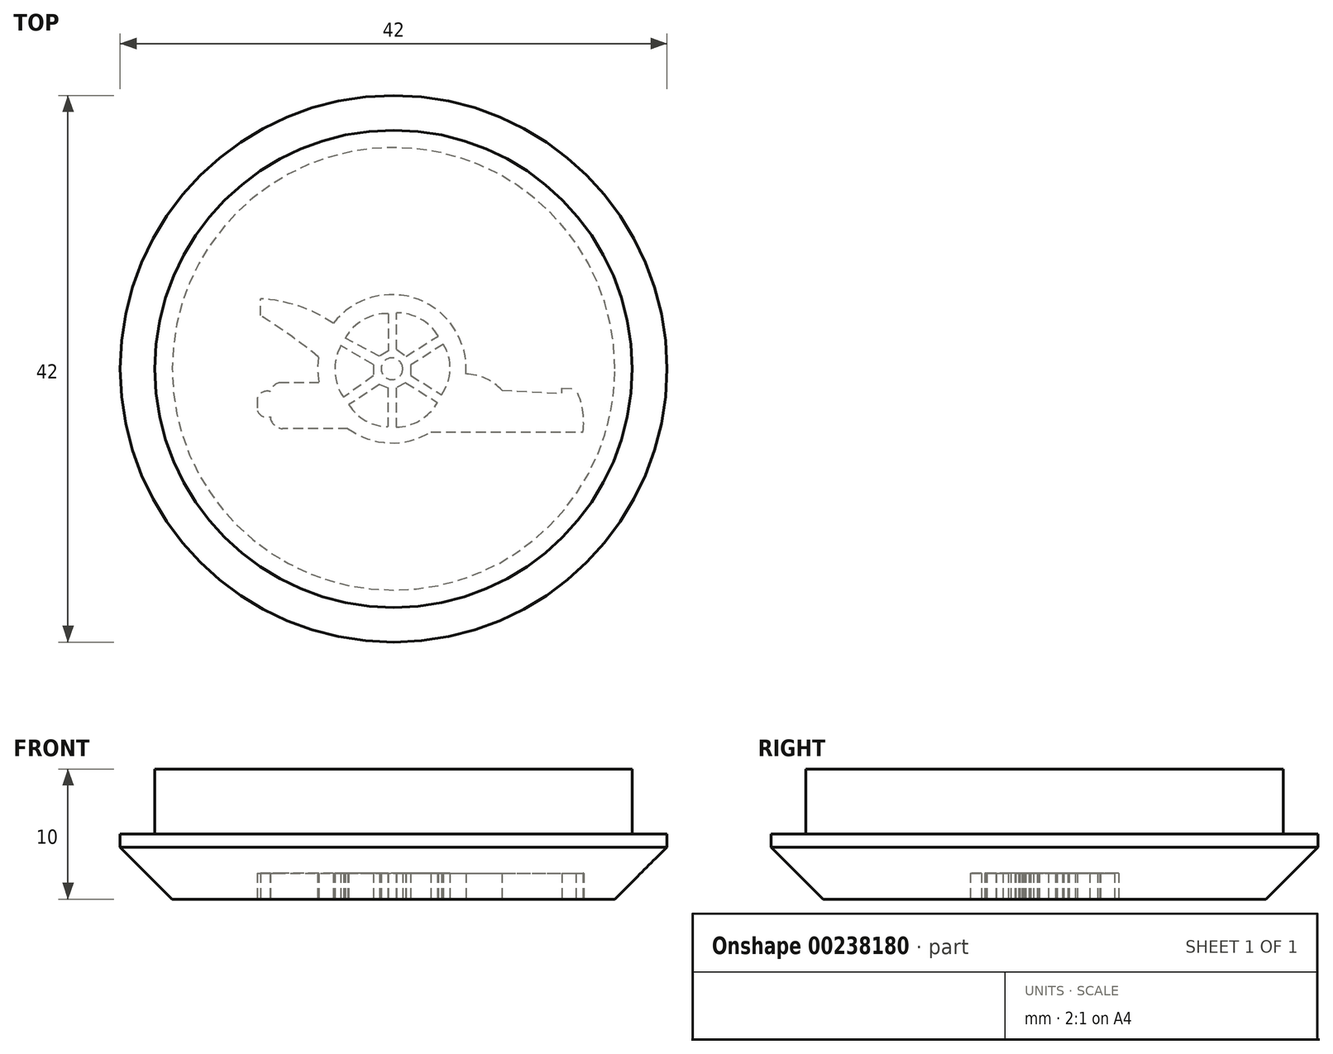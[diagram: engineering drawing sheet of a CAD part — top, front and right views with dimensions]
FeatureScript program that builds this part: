
annotation { "Feature Type Name" : "Feature", "Feature Type Description" : "" }
export const myFeature = defineFeature(function(context is Context, id is Id, definition is map)
    precondition{}
    {
        {
            var Q0;
            Q0=qCreatedBy(makeId("Top.planeOp"),FACE);
            var sketch = newSketch(context, id + "F0", { "sketchPlane" : qUnion([Q0])});
            skCircle(sketch, "E0", {"center": v(0, 0) * mm, "radius": 21 * mm});
            skSolve(sketch);
        }
        {
            var Q0;
            Q0=makeQuery(id+"F0.imprint","IMPRINT",FACE,{"disambiguationData":[TD([[makeQuery(id+"F0.imprint","IMPRINT",EDGE,{"derivedFrom":sQuery(id+"F0.wireOp",EDGE,"E0")}),1.0]])]});
            extrude(context, id + "F1", {"entities" : qUnion([Q0]), "depth" : 5 * mm, "offsetDistance" : 25 * mm});
        }
        {
            var Q0;
            Q0=makeQuery(id+"F1.opExtrude","CAP_FACE",FACE,{"disambiguationData":[OSD([sQuery(id+"F0.wireOp",EDGE,"E0")])],"isStart":false});
            var sketch = newSketch(context, id + "F2", { "sketchPlane" : qUnion([Q0])});
            skCircle(sketch, "E1", {"center": v(0, 0) * mm, "radius": 18.33 * mm});
            skSolve(sketch);
        }
        {
            var Q0;
            Q0=makeQuery(id+"F2.imprint","IMPRINT",FACE,{"disambiguationData":[TD([[makeQuery(id+"F2.imprint","IMPRINT",EDGE,{"derivedFrom":sQuery(id+"F2.wireOp",EDGE,"E1")}),1.0]])]});
            extrude(context, id + "F3", {"entities" : qUnion([Q0]), "operationType" : NewBodyOperationType.ADD, "depth" : 5 * mm, "offsetDistance" : 25 * mm});
        }
        {
            var Q0;
            Q0=makeQuery(id+"F1.opExtrude","CAP_FACE",FACE,{"disambiguationData":[OSD([sQuery(id+"F0.wireOp",EDGE,"E0")])],"isStart":true});
            var sketch = newSketch(context, id + "F4", { "sketchPlane" : qUnion([Q0])});
            skLineSegment(sketch, "E2", {"start": v(-5.73, 1.06) * mm, "end": v(-8.6, 1.06) * mm});
            skLineSegment(sketch, "E3", {"start": v(-3.5, 4.6) * mm, "end": v(-8.52, 4.6) * mm});
            skArc(sketch, "E4", {"start": v(-9.47, 1.74) * mm, "mid": v(-9.15, 1.25) * mm, "end": v(-8.6, 1.06) * mm});
            skArc(sketch, "E5", {"start": v(-8.52, 4.6) * mm, "mid": v(-9.18, 4.33) * mm, "end": v(-9.47, 3.69) * mm});
            skLineSegment(sketch, "E6", {"start": v(-10.48, 2.26) * mm, "end": v(-10.48, 3.2) * mm});
            skArc(sketch, "E7", {"start": v(-10.48, 2.26) * mm, "mid": v(-10.07, 1.81) * mm, "end": v(-9.47, 1.74) * mm});
            skArc(sketch, "E8", {"start": v(-9.47, 3.69) * mm, "mid": v(-10.07, 3.65) * mm, "end": v(-10.48, 3.2) * mm});
            skCircle(sketch, "E9", {"center": v(-0.13, 0) * mm, "radius": 5.7 * mm});
            skCircle(sketch, "E10", {"center": v(-0.13, 0) * mm, "radius": 0.83 * mm});
            skArc(sketch, "E11", {"start": v(-10.22, -4.09) * mm, "mid": v(-7.94, -2.56) * mm, "end": v(-5.76, -0.9) * mm});
            skLineSegment(sketch, "E12", {"start": v(-10.22, -4.09) * mm, "end": v(-10.22, -5.37) * mm});
            skArc(sketch, "E13", {"start": v(-10.22, -5.37) * mm, "mid": v(-7.3, -4.82) * mm, "end": v(-4.64, -3.49) * mm});
            skArc(sketch, "E14", {"start": v(5.56, 0.4) * mm, "mid": v(7.08, 0.74) * mm, "end": v(8.33, 1.66) * mm});
            skLineSegment(sketch, "E15", {"start": v(8.33, 1.66) * mm, "end": v(12.92, 1.88) * mm});
            skLineSegment(sketch, "E16", {"start": v(12.92, 1.88) * mm, "end": v(12.94, 1.49) * mm});
            skLineSegment(sketch, "E17", {"start": v(12.94, 1.49) * mm, "end": v(14, 1.54) * mm});
            skLineSegment(sketch, "E18", {"start": v(2.88, 4.84) * mm, "end": v(14.55, 4.84) * mm});
            skArc(sketch, "E19", {"start": v(14, 1.54) * mm, "mid": v(14.52, 3.15) * mm, "end": v(14.55, 4.84) * mm});
            skArc(sketch, "E20", {"start": v(-3.26, -2.55) * mm, "mid": v(-2.14, -3.5) * mm, "end": v(-0.77, -4.06) * mm});
            skLineSegment(sketch, "E21", {"start": v(-1.56, -0.31) * mm, "end": v(-1.56, 0.55) * mm});
            skLineSegment(sketch, "E22", {"start": v(-1.56, 0.55) * mm, "end": v(-3.84, 2.2) * mm});
            skLineSegment(sketch, "E23", {"start": v(-1.56, -0.31) * mm, "end": v(-4.04, -1.78) * mm});
            skLineSegment(sketch, "E24", {"start": v(0.22, -1.49) * mm, "end": v(0.22, -4.29) * mm});
            skLineSegment(sketch, "E25", {"start": v(0.22, -1.49) * mm, "end": v(0.96, -0.95) * mm});
            skLineSegment(sketch, "E26", {"start": v(0.96, -0.95) * mm, "end": v(3.43, -2.53) * mm});
            skLineSegment(sketch, "E27", {"start": v(-0.4, -4.24) * mm, "end": v(-0.4, -1.37) * mm});
            skLineSegment(sketch, "E28", {"start": v(-0.4, -1.37) * mm, "end": v(-1.08, -0.95) * mm});
            skLineSegment(sketch, "E29", {"start": v(-1.08, -0.95) * mm, "end": v(-3.7, -2.37) * mm});
            skLineSegment(sketch, "E30", {"start": v(-3.26, -2.55) * mm, "end": v(-1.24, -1.28) * mm});
            skLineSegment(sketch, "E31", {"start": v(-1.24, -1.28) * mm, "end": v(-0.8, -1.54) * mm});
            skLineSegment(sketch, "E32", {"start": v(-0.8, -1.54) * mm, "end": v(-0.77, -4.06) * mm});
            skLineSegment(sketch, "E33", {"start": v(0.63, -3.91) * mm, "end": v(0.54, -1.56) * mm});
            skLineSegment(sketch, "E34", {"start": v(0.54, -1.56) * mm, "end": v(0.92, -1.3) * mm});
            skLineSegment(sketch, "E35", {"start": v(0.92, -1.3) * mm, "end": v(2.97, -2.54) * mm});
            skLineSegment(sketch, "E36", {"start": v(3.69, -1.53) * mm, "end": v(1.64, -0.17) * mm});
            skLineSegment(sketch, "E37", {"start": v(1.64, -0.17) * mm, "end": v(1.64, 0.32) * mm});
            skLineSegment(sketch, "E38", {"start": v(1.64, 0.32) * mm, "end": v(3.67, 1.62) * mm});
            skLineSegment(sketch, "E39", {"start": v(1.33, -0.29) * mm, "end": v(1.33, 0.5) * mm});
            skLineSegment(sketch, "E40", {"start": v(1.33, 0.5) * mm, "end": v(3.69, 2) * mm});
            skLineSegment(sketch, "E41", {"start": v(3.82, -1.9) * mm, "end": v(1.33, -0.29) * mm});
            skLineSegment(sketch, "E42", {"start": v(-1.77, -0.15) * mm, "end": v(-1.77, 0.46) * mm});
            skLineSegment(sketch, "E43", {"start": v(-1.77, 0.46) * mm, "end": v(-3.75, 1.8) * mm});
            skLineSegment(sketch, "E44", {"start": v(-1.77, -0.15) * mm, "end": v(-3.87, -1.34) * mm});
            skLineSegment(sketch, "E45", {"start": v(-1.05, 1.5) * mm, "end": v(-0.8, 1.6) * mm});
            skLineSegment(sketch, "E46", {"start": v(-0.8, 1.6) * mm, "end": v(-0.8, 4.08) * mm});
            skLineSegment(sketch, "E47", {"start": v(-1.05, 1.5) * mm, "end": v(-3, 2.8) * mm});
            skLineSegment(sketch, "E48", {"start": v(-1.07, 1.2) * mm, "end": v(-0.44, 1.44) * mm});
            skLineSegment(sketch, "E49", {"start": v(-0.44, 1.44) * mm, "end": v(-0.44, 4.45) * mm});
            skLineSegment(sketch, "E50", {"start": v(-1.07, 1.2) * mm, "end": v(-3.44, 2.77) * mm});
            skLineSegment(sketch, "E51", {"start": v(0.93, 1.08) * mm, "end": v(3.37, 2.6) * mm});
            skLineSegment(sketch, "E52", {"start": v(0.93, 1.08) * mm, "end": v(0.2, 1.46) * mm});
            skLineSegment(sketch, "E53", {"start": v(0.2, 1.46) * mm, "end": v(0.2, 4.48) * mm});
            skLineSegment(sketch, "E54", {"start": v(0.94, 1.44) * mm, "end": v(0.6, 1.6) * mm});
            skLineSegment(sketch, "E55", {"start": v(0.6, 1.6) * mm, "end": v(0.6, 4.14) * mm});
            skLineSegment(sketch, "E56", {"start": v(0.94, 1.44) * mm, "end": v(2.99, 2.73) * mm});
            skArc(sketch, "E57", {"start": v(-3.75, 1.8) * mm, "mid": v(-4.17, 0.24) * mm, "end": v(-3.87, -1.34) * mm});
            skArc(sketch, "E58", {"start": v(-3.84, 2.2) * mm, "mid": v(-4.5, 0.23) * mm, "end": v(-4.04, -1.78) * mm});
            skArc(sketch, "E59", {"start": v(-3.7, -2.37) * mm, "mid": v(-2.31, -3.76) * mm, "end": v(-0.4, -4.24) * mm});
            skArc(sketch, "E60", {"start": v(0.22, -4.29) * mm, "mid": v(2.06, -3.83) * mm, "end": v(3.43, -2.53) * mm});
            skArc(sketch, "E61", {"start": v(0.63, -3.91) * mm, "mid": v(1.97, -3.52) * mm, "end": v(2.97, -2.54) * mm});
            skArc(sketch, "E62", {"start": v(3.69, -1.53) * mm, "mid": v(3.98, 0.05) * mm, "end": v(3.67, 1.62) * mm});
            skArc(sketch, "E63", {"start": v(3.82, -1.9) * mm, "mid": v(4.33, 0.07) * mm, "end": v(3.69, 2) * mm});
            skArc(sketch, "E64", {"start": v(2.99, 2.73) * mm, "mid": v(1.92, 3.64) * mm, "end": v(0.6, 4.14) * mm});
            skArc(sketch, "E65", {"start": v(3.37, 2.6) * mm, "mid": v(2.03, 3.96) * mm, "end": v(0.2, 4.48) * mm});
            skArc(sketch, "E66", {"start": v(-0.8, 4.08) * mm, "mid": v(-2.04, 3.67) * mm, "end": v(-3, 2.8) * mm});
            skArc(sketch, "E67", {"start": v(-0.44, 4.45) * mm, "mid": v(-2.15, 4) * mm, "end": v(-3.44, 2.77) * mm});
            skSolve(sketch);
        }
        {
            var Q0;
            {var subQ1=sQuery(id+"F4.wireOp",EDGE,"E2");Q0=makeQuery(id+"F4.imprint","IMPRINT",FACE,{"disambiguationData":[TD([[makeQuery(id+"F4.imprint","IMPRINT",EDGE,{"derivedFrom":subQ1}),-1.0]])]});}
            var Q1;
            Q1=makeQuery(id+"F4.imprint","IMPRINT",FACE,{"disambiguationData":[TD([[makeQuery(id+"F4.imprint","IMPRINT",EDGE,{"derivedFrom":sQuery(id+"F4.wireOp",EDGE,"E10")}),-1.0]])]});
            var Q2;
            {var subQ0=sQuery(id+"F4.wireOp",EDGE,"E11");Q2=makeQuery(id+"F4.imprint","IMPRINT",FACE,{"disambiguationData":[TD([[makeQuery(id+"F4.imprint","IMPRINT",EDGE,{"derivedFrom":subQ0}),-1.0]])]});}
            var Q3;
            {var subQ0=sQuery(id+"F4.wireOp",EDGE,"E14");Q3=makeQuery(id+"F4.imprint","IMPRINT",FACE,{"disambiguationData":[TD([[makeQuery(id+"F4.imprint","IMPRINT",EDGE,{"derivedFrom":subQ0}),1.0]])]});}
            extrude(context, id + "F5", {"entities" : qUnion([Q0, Q1, Q2, Q3]), "operationType" : NewBodyOperationType.REMOVE, "oppositeDirection" : true, "depth" : 2 * mm, "offsetDistance" : 25 * mm});
        }
        {
            var Q0;
            Q0=makeQuery(id+"F1.opExtrude","CAP_EDGE",EDGE,{"disambiguationData":[OSD([sQuery(id+"F0.wireOp",EDGE,"E0")])],"isStart":true});
            chamfer(context, id + "F6", {"entities" : qUnion([Q0]), "width" : 4 * mm, "tangentPropagation" : true});
        }
    });
